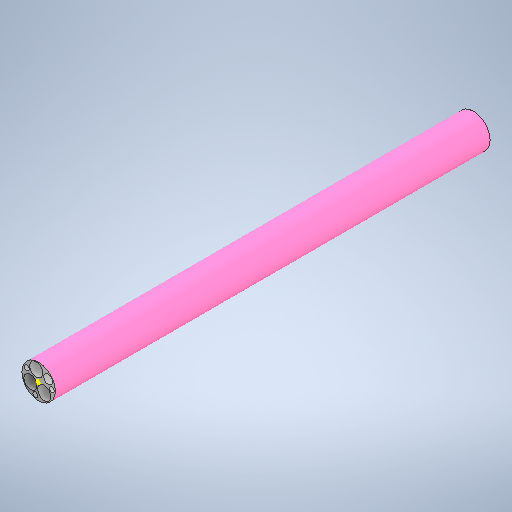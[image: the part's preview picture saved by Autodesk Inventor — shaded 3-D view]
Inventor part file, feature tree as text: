
AUTODESK INVENTOR PART (.ipt)
format: ipt  version: 2025.2 (Build 292293000, 293)  size: 256,000 bytes
history: native  units: mm
features: sketch x3, extrude x1
ambient origin geometry x8: Origin, YZ Plane, XZ Plane, XY Plane, X Axis, Y Axis, Z Axis, Center Point
bodies: Solid1 (feature_tree)
feature tree (4):
  extrude  "Extrusion1"  Depth=10.0mm
  sketch  "Sketch2"  dims[d2=4.0mm]
  sketch  "Sketch3"  dims[d3=4.0mm d5=2.7mm d6=1.5mm d7=1.5mm d8=1.5mm d9=130.0mm d10=0.0mm]
  sketch  "Sketch1"  dims[d0=10.0mm d1=4.0mm]
